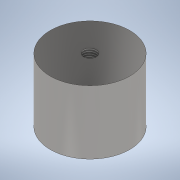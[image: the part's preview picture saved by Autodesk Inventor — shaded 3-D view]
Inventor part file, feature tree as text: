
AUTODESK INVENTOR PART (.ipt)
format: ipt  version: 2022 (Build 260153000, 153)  size: 102,912 bytes
history: native  units: in
note: dims shown in document units (in); Inventor stores cm internally (conversion verified against a paired STEP export)
features: sketch x2, extrude x1, hole x1, thread x1
ambient origin geometry x8: Origin, YZ Plane, XZ Plane, XY Plane, X Axis, Y Axis, Z Axis, Center Point
bodies: Solid1 (feature_tree)
feature tree (5):
  extrude  "Extrusion1"  Depth=0.7874in TaperAngle=0.0deg
  hole  "Hole1"  [1 undecoded]
  thread  "Thread1"  [1 undecoded]
  sketch  "Sketch1"  dims[d0=0.9843in d1=0.7874in d2=0.0in]
  sketch  "Sketch2"  dims[d3=0.1575in d4=0.2362in d5=1.0039in d6=0.0591in d7=90.0deg d8=0.315in d9=0.8108in d10=0.7874in d11=0.0in]
note: 2 required parameter values undecoded (feature->parameter linkage not recoverable at this tier; creation-order binding heuristic only, values carry confidence <= 0.55)
